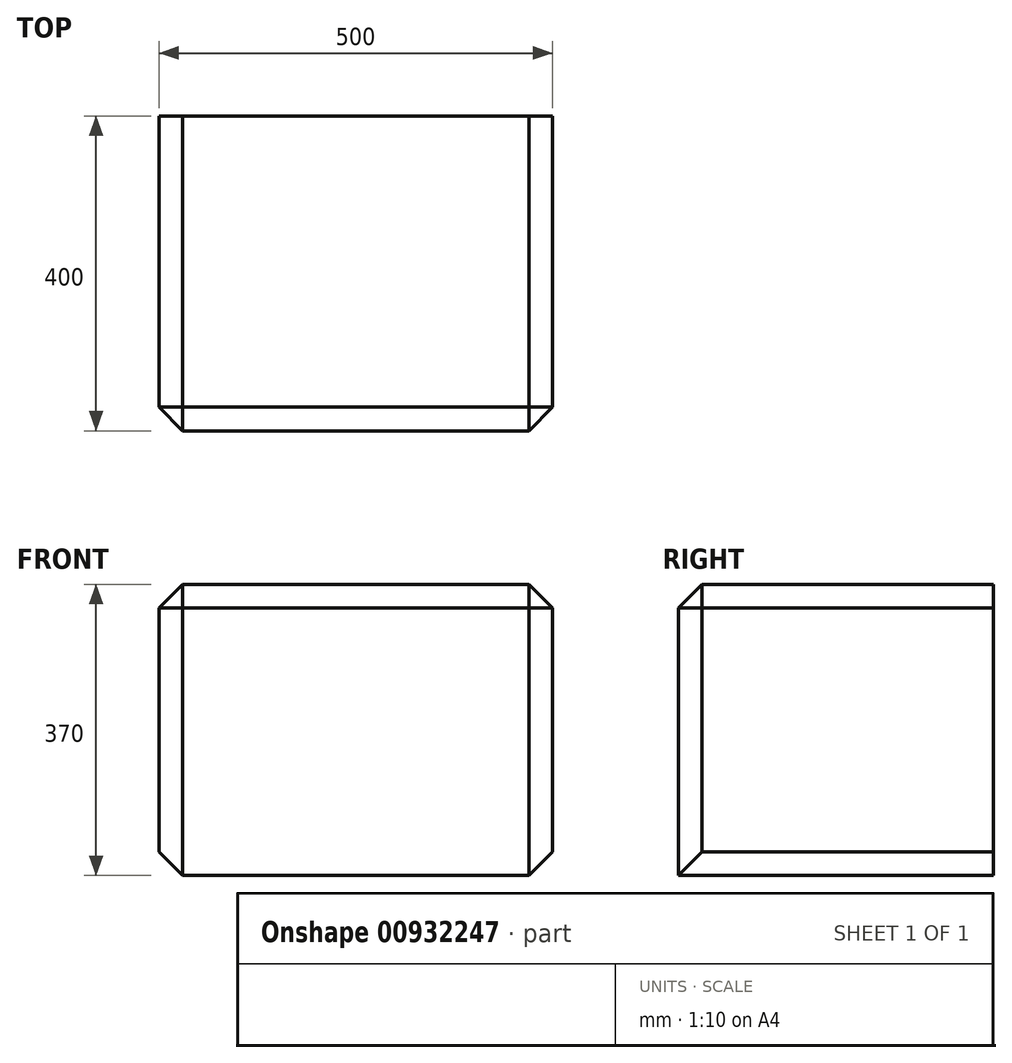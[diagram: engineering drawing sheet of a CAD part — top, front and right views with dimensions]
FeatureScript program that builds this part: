
annotation { "Feature Type Name" : "Feature", "Feature Type Description" : "" }
export const myFeature = defineFeature(function(context is Context, id is Id, definition is map)
    precondition{}
    {
        {
            var Q0;
            Q0=qCreatedBy(makeId("Top.planeOp"),FACE);
            var sketch = newSketch(context, id + "F0", { "sketchPlane" : qUnion([Q0])});
            skLineSegment(sketch, "E0.bottom", {"start": v(250, -200) * mm, "end": v(-250, -200) * mm});
            skLineSegment(sketch, "E0.top", {"start": v(250, 200) * mm, "end": v(-250, 200) * mm});
            skLineSegment(sketch, "E0.left", {"start": v(250, -200) * mm, "end": v(250, 200) * mm});
            skLineSegment(sketch, "E0.right", {"start": v(-250, -200) * mm, "end": v(-250, 200) * mm});
            skPoint(sketch, "E0.middle", {"position": v(0, 0) * mm});
            skLineSegment(sketch, "E1", {"start": v(-250, 150) * mm, "end": v(250, 150) * mm});
            skSolve(sketch);
        }
        {
            var Q0;
            {var subQ0=sQuery(id+"F0.wireOp",EDGE,"E0.bottom");Q0=makeQuery(id+"F0.imprint","IMPRINT",FACE,{"disambiguationData":[TD([[makeQuery(id+"F0.imprint","IMPRINT",EDGE,{"derivedFrom":subQ0}),-1.0]])]});}
            var Q1;
            {var subQ0=sQuery(id+"F0.wireOp",EDGE,"E0.top");Q1=makeQuery(id+"F0.imprint","IMPRINT",FACE,{"disambiguationData":[TD([[makeQuery(id+"F0.imprint","IMPRINT",EDGE,{"derivedFrom":subQ0}),1.0]])]});}
            extrude(context, id + "F1", {"entities" : qUnion([Q0, Q1]), "depth" : 370 * mm, "offsetDistance" : 25 * mm});
        }
        {
            var Q0;
            Q0=makeQuery(id+"F1.opExtrude","CAP_EDGE",EDGE,{"disambiguationData":[OSD([sQuery(id+"F0.wireOp",EDGE,"E0.right")])],"isStart":false});
            var Q1;
            Q1=makeQuery(id+"F1.opExtrude","CAP_EDGE",EDGE,{"disambiguationData":[OSD([sQuery(id+"F0.wireOp",EDGE,"E0.bottom")])],"isStart":false});
            var Q2;
            Q2=makeQuery(id+"F1.opExtrude","CAP_EDGE",EDGE,{"disambiguationData":[OSD([sQuery(id+"F0.wireOp",EDGE,"E0.left")])],"isStart":false});
            var Q3;
            Q3=makeQuery(id+"F1.opExtrude","SWEPT_EDGE",EDGE,{"disambiguationData":[OSD([sQuery(id+"F0.wireOp",EDGE,"E0.bottom"),sQuery(id+"F0.wireOp",EDGE,"E0.right")])]});
            var Q4;
            Q4=makeQuery(id+"F1.opExtrude","SWEPT_EDGE",EDGE,{"disambiguationData":[OSD([sQuery(id+"F0.wireOp",EDGE,"E0.bottom"),sQuery(id+"F0.wireOp",EDGE,"E0.left")])]});
            var Q5;
            Q5=makeQuery(id+"F1.opExtrude","CAP_EDGE",EDGE,{"disambiguationData":[OSD([sQuery(id+"F0.wireOp",EDGE,"E0.left")])],"isStart":true});
            var Q6;
            Q6=makeQuery(id+"F1.opExtrude","CAP_EDGE",EDGE,{"disambiguationData":[OSD([sQuery(id+"F0.wireOp",EDGE,"E0.right")])],"isStart":true});
            chamfer(context, id + "F2", {"entities" : qUnion([Q0, Q1, Q2, Q3, Q4, Q5, Q6]), "width" : 30 * mm, "tangentPropagation" : true});
        }
    });
